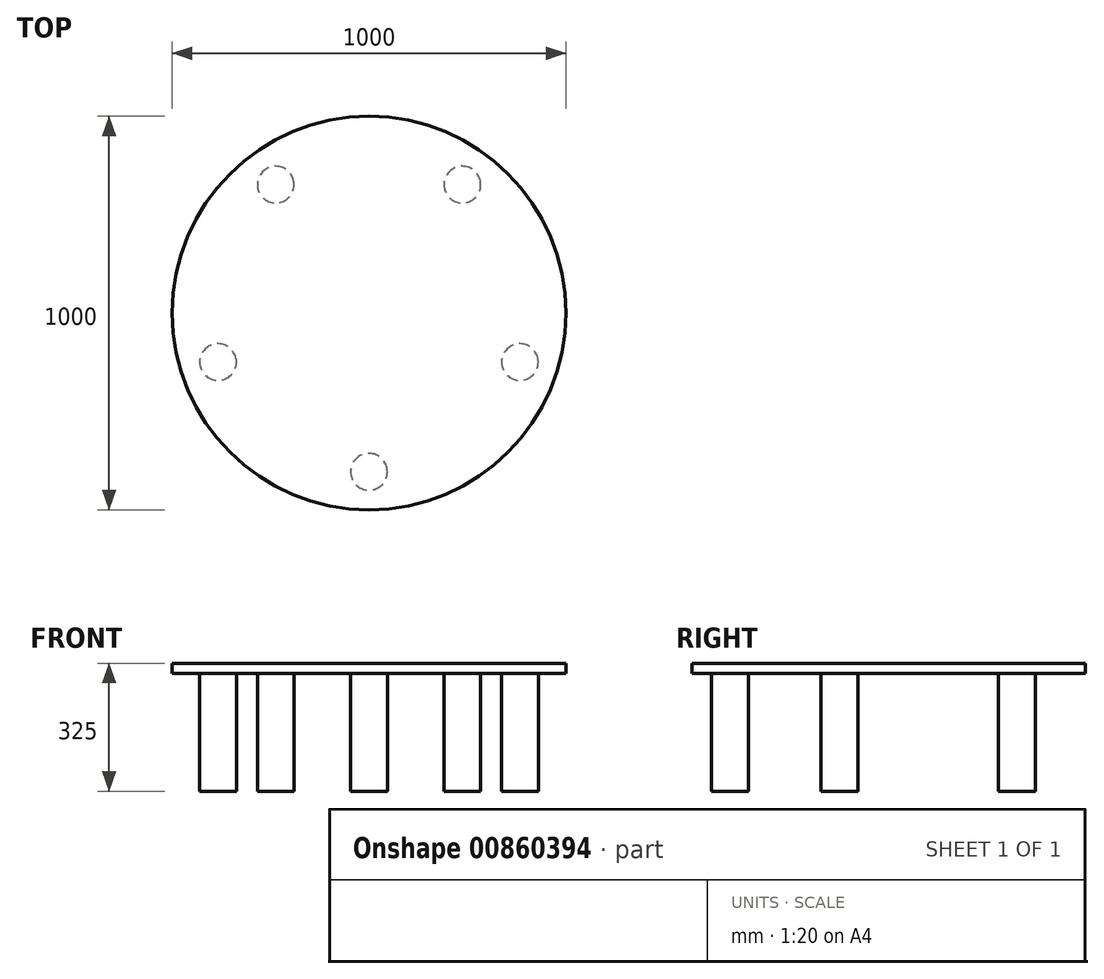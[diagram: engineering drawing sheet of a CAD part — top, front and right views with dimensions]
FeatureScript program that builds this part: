
annotation { "Feature Type Name" : "Feature", "Feature Type Description" : "" }
export const myFeature = defineFeature(function(context is Context, id is Id, definition is map)
    precondition{}
    {
        {
            var Q0;
            Q0=qCreatedBy(makeId("Top.planeOp"),FACE);
            var sketch = newSketch(context, id + "F0", { "sketchPlane" : qUnion([Q0])});
            skCircle(sketch, "E0", {"center": v(0, 0) * mm, "radius": 500 * mm});
            skSolve(sketch);
        }
        {
            var Q0;
            Q0=makeQuery(id+"F0.imprint","IMPRINT",FACE,{"disambiguationData":[TD([[makeQuery(id+"F0.imprint","IMPRINT",EDGE,{"derivedFrom":sQuery(id+"F0.wireOp",EDGE,"E0")}),1.0]])]});
            var sketch = newSketch(context, id + "F1", { "sketchPlane" : qUnion([Q0])});
            skCircle(sketch, "E1", {"center": v(0, -403.25) * mm, "radius": 46.69 * mm});
            skSolve(sketch);
        }
        {
            var Q0;
            Q0=makeQuery(id+"F0.imprint","IMPRINT",FACE,{"disambiguationData":[TD([[makeQuery(id+"F0.imprint","IMPRINT",EDGE,{"derivedFrom":sQuery(id+"F0.wireOp",EDGE,"E0")}),1.0]])]});
            extrude(context, id + "F2", {"entities" : qUnion([Q0]), "depth" : 25 * mm, "offsetDistance" : 25 * mm});
        }
        {
            var Q0;
            Q0=makeQuery(id+"F1.imprint","IMPRINT",FACE,{"disambiguationData":[TD([[makeQuery(id+"F1.imprint","IMPRINT",EDGE,{"derivedFrom":sQuery(id+"F1.wireOp",EDGE,"E1")}),1.0]])]});
            extrude(context, id + "F3", {"entities" : qUnion([Q0]), "oppositeDirection" : true, "depth" : 300 * mm, "offsetDistance" : 25 * mm});
        }
        {
            var Q0;
            Q0=makeQuery(id+"F3.opExtrude","SWEPT_BODY",BODY,{"disambiguationData":[OSD([sQuery(id+"F1.wireOp",EDGE,"E1")])]});
            var Q1;
            Q1=makeQuery(id+"F2.opExtrude","CAP_EDGE",EDGE,{"disambiguationData":[OSD([sQuery(id+"F0.wireOp",EDGE,"E0")])],"isStart":true});
            circularPattern(context, id + "F4", {"operationType" : NewBodyOperationType.ADD, "entities" : qUnion([Q0]), "axis" : qUnion([Q1]), "angle" : 360 * degree, "instanceCount" : 5, "equalSpace" : true});
        }
    });
